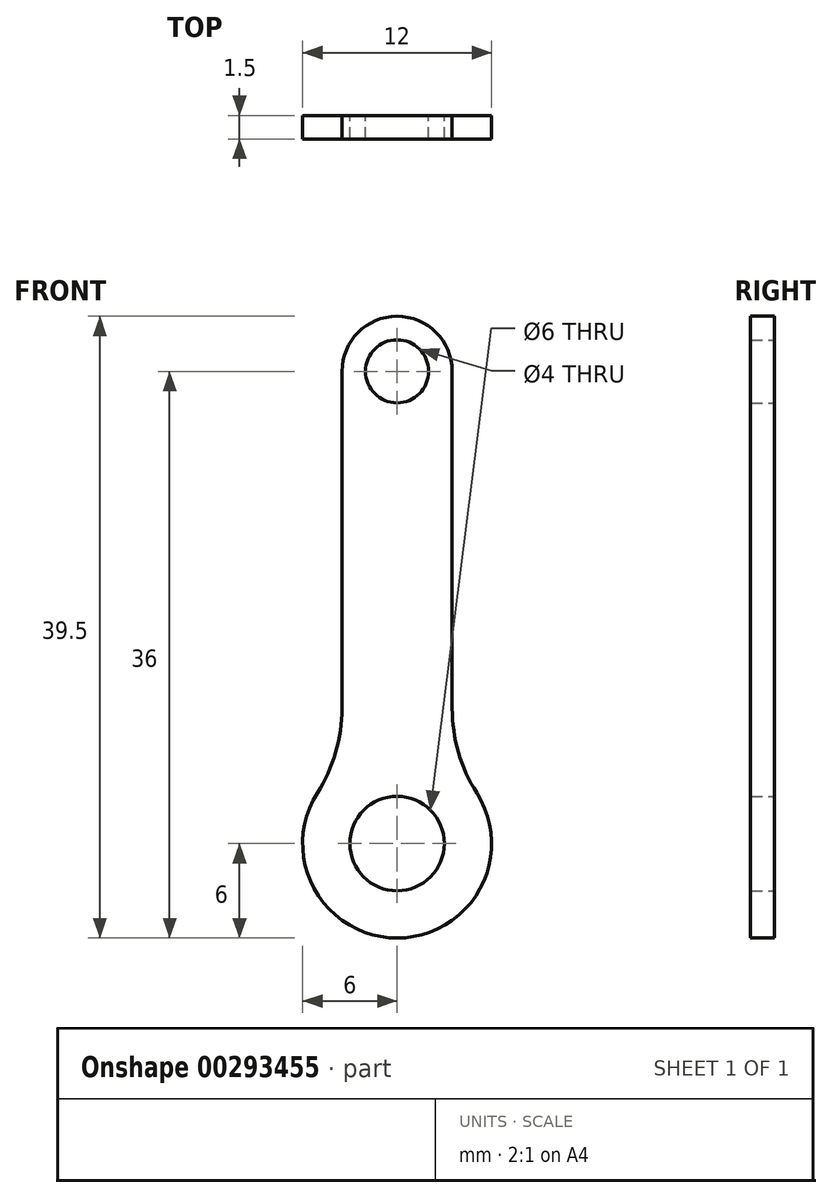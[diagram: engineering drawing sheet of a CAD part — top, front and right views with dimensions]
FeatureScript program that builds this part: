
annotation { "Feature Type Name" : "Feature", "Feature Type Description" : "" }
export const myFeature = defineFeature(function(context is Context, id is Id, definition is map)
    precondition{}
    {
        {
            var Q0;
            Q0=qCreatedBy(makeId("Front.planeOp"),FACE);
            var sketch = newSketch(context, id + "F0", { "sketchPlane" : qUnion([Q0])});
            skCircle(sketch, "E0", {"center": v(0, 0) * mm, "radius": 3 * mm});
            skCircle(sketch, "E1", {"center": v(0, 30) * mm, "radius": 2 * mm});
            skLineSegment(sketch, "E2", {"start": v(-3.5, 30) * mm, "end": v(-3.5, 8.59) * mm});
            skLineSegment(sketch, "E3", {"start": v(3.5, 30) * mm, "end": v(3.5, 8.59) * mm});
            skPoint(sketch, "E4.visualSharp", {"position": v(-3.5, 4.87) * mm});
            skPoint(sketch, "E5.visualSharp", {"position": v(3.5, 4.87) * mm});
            skArc(sketch, "E6", {"start": v(3.5, 30) * mm, "mid": v(0, 33.5) * mm, "end": v(-3.5, 30) * mm});
            skLineSegment(sketch, "E7", {"start": v(0, -11.8) * mm, "end": v(0, 8.32) * mm, "construction": true});
            skArc(sketch, "E8", {"start": v(-5.06, 3.22) * mm, "mid": v(0, -6) * mm, "end": v(5.06, 3.22) * mm});
            skArc(sketch, "E9.filletArc", {"start": v(-5.06, 3.22) * mm, "mid": v(-3.9, 5.8) * mm, "end": v(-3.5, 8.59) * mm});
            skArc(sketch, "E10.filletArc", {"start": v(3.5, 8.59) * mm, "mid": v(3.9, 5.8) * mm, "end": v(5.06, 3.22) * mm});
            skSolve(sketch);
        }
        {
            var Q0;
            Q0=makeQuery(id+"F0.imprint","IMPRINT",FACE,{"disambiguationData":[TD([[makeQuery(id+"F0.imprint","IMPRINT",EDGE,{"derivedFrom":sQuery(id+"F0.wireOp",EDGE,"E0")}),-1.0]])]});
            extrude(context, id + "F1", {"entities" : qUnion([Q0]), "depth" : 1.5 * mm});
        }
    });
